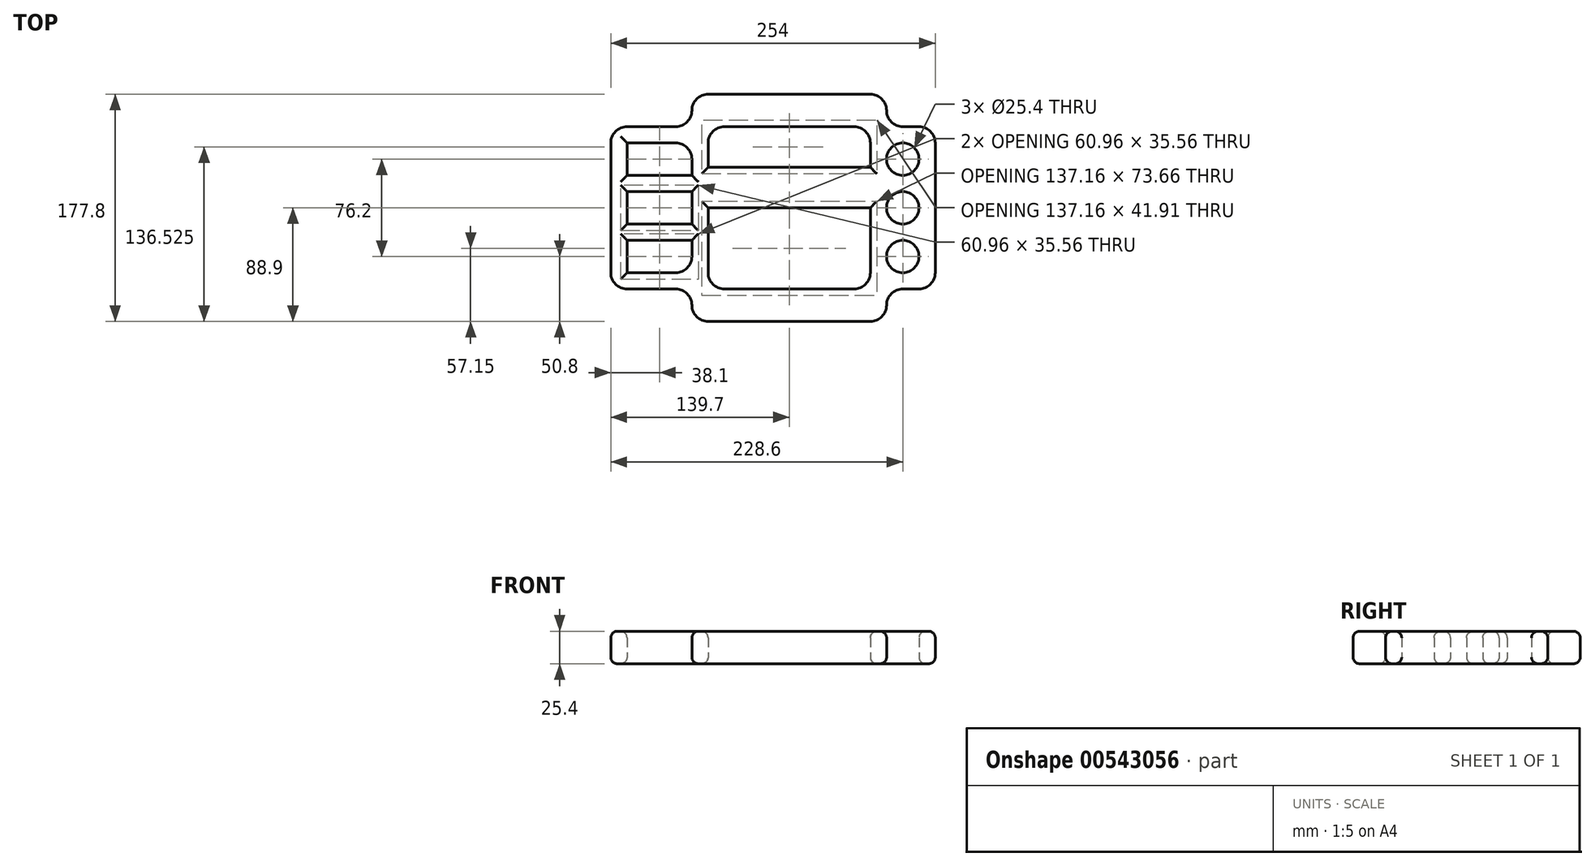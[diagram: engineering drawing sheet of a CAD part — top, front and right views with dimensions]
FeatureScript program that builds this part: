
annotation { "Feature Type Name" : "Feature", "Feature Type Description" : "" }
export const myFeature = defineFeature(function(context is Context, id is Id, definition is map)
    precondition{}
    {
        {
            var Q0;
            Q0=qCreatedBy(makeId("Top.planeOp"),FACE);
            var sketch = newSketch(context, id + "F0", { "sketchPlane" : qUnion([Q0])});
            skLineSegment(sketch, "E0", {"start": v(0, 12.7) * mm, "end": v(0, 12.7) * mm});
            skLineSegment(sketch, "E1", {"start": v(-12.7, 25.4) * mm, "end": v(-50.8, 25.4) * mm});
            skLineSegment(sketch, "E2", {"start": v(-63.5, 38.1) * mm, "end": v(-63.5, 139.7) * mm});
            skLineSegment(sketch, "E3", {"start": v(-50.8, 152.4) * mm, "end": v(-12.7, 152.4) * mm});
            skLineSegment(sketch, "E4", {"start": v(0, 165.1) * mm, "end": v(0, 165.1) * mm});
            skLineSegment(sketch, "E5", {"start": v(12.7, 177.8) * mm, "end": v(139.7, 177.8) * mm});
            skLineSegment(sketch, "E6", {"start": v(152.4, 165.1) * mm, "end": v(152.4, 165.1) * mm});
            skLineSegment(sketch, "E7", {"start": v(165.1, 152.4) * mm, "end": v(177.8, 152.4) * mm});
            skLineSegment(sketch, "E8", {"start": v(190.5, 139.7) * mm, "end": v(190.5, 38.1) * mm});
            skLineSegment(sketch, "E9", {"start": v(177.8, 25.4) * mm, "end": v(165.1, 25.4) * mm});
            skLineSegment(sketch, "E10", {"start": v(152.4, 12.7) * mm, "end": v(152.4, 12.7) * mm});
            skLineSegment(sketch, "E11", {"start": v(139.7, 0) * mm, "end": v(12.7, 0) * mm});
            skPoint(sketch, "E12.visualSharp", {"position": v(0, 177.8) * mm});
            skArc(sketch, "E12.filletArc", {"start": v(12.7, 177.8) * mm, "mid": v(3.72, 174.08) * mm, "end": v(0, 165.1) * mm});
            skPoint(sketch, "E13.visualSharp", {"position": v(152.4, 177.8) * mm});
            skArc(sketch, "E13.filletArc", {"start": v(152.4, 165.1) * mm, "mid": v(148.68, 174.08) * mm, "end": v(139.7, 177.8) * mm});
            skPoint(sketch, "E14.visualSharp", {"position": v(152.4, 152.4) * mm});
            skArc(sketch, "E14.filletArc", {"start": v(152.4, 165.1) * mm, "mid": v(156.12, 156.12) * mm, "end": v(165.1, 152.4) * mm});
            skPoint(sketch, "E15.visualSharp", {"position": v(190.5, 152.4) * mm});
            skArc(sketch, "E15.filletArc", {"start": v(190.5, 139.7) * mm, "mid": v(186.78, 148.68) * mm, "end": v(177.8, 152.4) * mm});
            skPoint(sketch, "E16.visualSharp", {"position": v(190.5, 25.4) * mm});
            skArc(sketch, "E16.filletArc", {"start": v(177.8, 25.4) * mm, "mid": v(186.78, 29.12) * mm, "end": v(190.5, 38.1) * mm});
            skPoint(sketch, "E17.visualSharp", {"position": v(152.4, 25.4) * mm});
            skArc(sketch, "E17.filletArc", {"start": v(165.1, 25.4) * mm, "mid": v(156.12, 21.68) * mm, "end": v(152.4, 12.7) * mm});
            skPoint(sketch, "E18.visualSharp", {"position": v(152.4, 0) * mm});
            skArc(sketch, "E18.filletArc", {"start": v(139.7, 0) * mm, "mid": v(148.68, 3.72) * mm, "end": v(152.4, 12.7) * mm});
            skPoint(sketch, "E19.visualSharp", {"position": v(0, 0) * mm});
            skArc(sketch, "E19.filletArc", {"start": v(0, 12.7) * mm, "mid": v(3.72, 3.72) * mm, "end": v(12.7, 0) * mm});
            skPoint(sketch, "E20.visualSharp", {"position": v(0, 25.4) * mm});
            skArc(sketch, "E20.filletArc", {"start": v(0, 12.7) * mm, "mid": v(-3.72, 21.68) * mm, "end": v(-12.7, 25.4) * mm});
            skPoint(sketch, "E21.visualSharp", {"position": v(-63.5, 25.4) * mm});
            skArc(sketch, "E21.filletArc", {"start": v(-63.5, 38.1) * mm, "mid": v(-59.78, 29.12) * mm, "end": v(-50.8, 25.4) * mm});
            skPoint(sketch, "E22.visualSharp", {"position": v(-63.5, 152.4) * mm});
            skArc(sketch, "E22.filletArc", {"start": v(-50.8, 152.4) * mm, "mid": v(-59.78, 148.68) * mm, "end": v(-63.5, 139.7) * mm});
            skPoint(sketch, "E23.visualSharp", {"position": v(0, 152.4) * mm});
            skArc(sketch, "E23.filletArc", {"start": v(-12.7, 152.4) * mm, "mid": v(-3.72, 156.12) * mm, "end": v(0, 165.1) * mm});
            skCircle(sketch, "E24", {"center": v(165.1, 88.9) * mm, "radius": 12.7 * mm});
            skPoint(sketch, "E24.centerSnap0", {"position": v(190.5, 88.9) * mm});
            skCircle(sketch, "E25", {"center": v(165.1, 127) * mm, "radius": 12.7 * mm});
            skCircle(sketch, "E26", {"center": v(165.1, 50.8) * mm, "radius": 12.7 * mm});
            skLineSegment(sketch, "E27.bottom", {"start": v(-50.8, 38.1) * mm, "end": v(-12.7, 38.1) * mm});
            skLineSegment(sketch, "E27.top", {"start": v(-50.8, 63.5) * mm, "end": v(0, 63.5) * mm});
            skLineSegment(sketch, "E27.left", {"start": v(-50.8, 38.1) * mm, "end": v(-50.8, 63.5) * mm});
            skLineSegment(sketch, "E27.right", {"start": v(0, 50.8) * mm, "end": v(0, 63.5) * mm});
            skLineSegment(sketch, "E28.bottom", {"start": v(-50.8, 101.6) * mm, "end": v(0, 101.6) * mm});
            skLineSegment(sketch, "E28.top", {"start": v(-50.8, 76.2) * mm, "end": v(0, 76.2) * mm});
            skLineSegment(sketch, "E28.left", {"start": v(-50.8, 101.6) * mm, "end": v(-50.8, 76.2) * mm});
            skLineSegment(sketch, "E28.right", {"start": v(0, 101.6) * mm, "end": v(0, 76.2) * mm});
            skLineSegment(sketch, "E29.bottom", {"start": v(-50.8, 139.7) * mm, "end": v(-12.7, 139.7) * mm});
            skLineSegment(sketch, "E29.top", {"start": v(-50.8, 114.3) * mm, "end": v(0, 114.3) * mm});
            skLineSegment(sketch, "E29.left", {"start": v(-50.8, 139.7) * mm, "end": v(-50.8, 114.3) * mm});
            skLineSegment(sketch, "E29.right", {"start": v(0, 127) * mm, "end": v(0, 114.3) * mm});
            skPoint(sketch, "E30.visualSharp", {"position": v(0, 139.7) * mm});
            skArc(sketch, "E30.filletArc", {"start": v(0, 127) * mm, "mid": v(-3.72, 135.98) * mm, "end": v(-12.7, 139.7) * mm});
            skPoint(sketch, "E31.visualSharp", {"position": v(0, 38.1) * mm});
            skArc(sketch, "E31.filletArc", {"start": v(-12.7, 38.1) * mm, "mid": v(-3.72, 41.82) * mm, "end": v(0, 50.8) * mm});
            skLineSegment(sketch, "E32.bottom", {"start": v(12.7, 120.65) * mm, "end": v(139.7, 120.65) * mm});
            skLineSegment(sketch, "E32.top", {"start": v(25.4, 152.4) * mm, "end": v(127, 152.4) * mm});
            skLineSegment(sketch, "E32.left", {"start": v(12.7, 120.65) * mm, "end": v(12.7, 139.7) * mm});
            skLineSegment(sketch, "E32.right", {"start": v(139.7, 120.65) * mm, "end": v(139.7, 139.7) * mm});
            skLineSegment(sketch, "E33.bottom", {"start": v(12.7, 88.9) * mm, "end": v(139.7, 88.9) * mm});
            skLineSegment(sketch, "E33.top", {"start": v(25.4, 25.4) * mm, "end": v(127, 25.4) * mm});
            skLineSegment(sketch, "E33.left", {"start": v(12.7, 88.9) * mm, "end": v(12.7, 38.1) * mm});
            skLineSegment(sketch, "E33.right", {"start": v(139.7, 88.9) * mm, "end": v(139.7, 38.1) * mm});
            skPoint(sketch, "E34.visualSharp", {"position": v(12.7, 25.4) * mm});
            skArc(sketch, "E34.filletArc", {"start": v(12.7, 38.1) * mm, "mid": v(16.42, 29.12) * mm, "end": v(25.4, 25.4) * mm});
            skPoint(sketch, "E35.visualSharp", {"position": v(139.7, 25.4) * mm});
            skArc(sketch, "E35.filletArc", {"start": v(127, 25.4) * mm, "mid": v(135.98, 29.12) * mm, "end": v(139.7, 38.1) * mm});
            skPoint(sketch, "E36.visualSharp", {"position": v(12.7, 152.4) * mm});
            skArc(sketch, "E36.filletArc", {"start": v(25.4, 152.4) * mm, "mid": v(16.42, 148.68) * mm, "end": v(12.7, 139.7) * mm});
            skPoint(sketch, "E37.visualSharp", {"position": v(139.7, 152.4) * mm});
            skArc(sketch, "E37.filletArc", {"start": v(139.7, 139.7) * mm, "mid": v(135.98, 148.68) * mm, "end": v(127, 152.4) * mm});
            skPoint(sketch, "E38.visualSharp", {"position": v(12.7, 88.9) * mm});
            skLineSegment(sketch, "E38.filletArc", {"start": v(12.7, 88.9) * mm, "end": v(12.7, 88.9) * mm});
            skSolve(sketch);
        }
        {
            var Q0;
            Q0=makeQuery(id+"F0.imprint","IMPRINT",FACE,{"disambiguationData":[TD([[makeQuery(id+"F0.imprint","IMPRINT",EDGE,{"derivedFrom":sQuery(id+"F0.wireOp",EDGE,"E1")}),-1.0]])]});
            extrude(context, id + "F1", {"entities" : qUnion([Q0]), "depth" : 25.4 * mm, "offsetDistance" : 25.4 * mm});
        }
        {
            var Q0;
            Q0=makeQuery(id+"F1.opExtrude","CAP_FACE",FACE,{"disambiguationData":[OSD([sQuery(id+"F0.wireOp",EDGE,"E1"),sQuery(id+"F0.wireOp",EDGE,"E2"),sQuery(id+"F0.wireOp",EDGE,"E3"),sQuery(id+"F0.wireOp",EDGE,"E5"),sQuery(id+"F0.wireOp",EDGE,"E7"),sQuery(id+"F0.wireOp",EDGE,"E8"),sQuery(id+"F0.wireOp",EDGE,"E9"),sQuery(id+"F0.wireOp",EDGE,"E11"),sQuery(id+"F0.wireOp",EDGE,"E12.filletArc"),sQuery(id+"F0.wireOp",EDGE,"E13.filletArc"),sQuery(id+"F0.wireOp",EDGE,"E14.filletArc"),sQuery(id+"F0.wireOp",EDGE,"E15.filletArc"),sQuery(id+"F0.wireOp",EDGE,"E16.filletArc"),sQuery(id+"F0.wireOp",EDGE,"E17.filletArc"),sQuery(id+"F0.wireOp",EDGE,"E18.filletArc"),sQuery(id+"F0.wireOp",EDGE,"E19.filletArc"),sQuery(id+"F0.wireOp",EDGE,"E20.filletArc"),sQuery(id+"F0.wireOp",EDGE,"E21.filletArc"),sQuery(id+"F0.wireOp",EDGE,"E22.filletArc"),sQuery(id+"F0.wireOp",EDGE,"E23.filletArc"),sQuery(id+"F0.wireOp",EDGE,"E24"),sQuery(id+"F0.wireOp",EDGE,"E25"),sQuery(id+"F0.wireOp",EDGE,"E26"),sQuery(id+"F0.wireOp",EDGE,"E27.bottom"),sQuery(id+"F0.wireOp",EDGE,"E27.top"),sQuery(id+"F0.wireOp",EDGE,"E27.left"),sQuery(id+"F0.wireOp",EDGE,"E27.right"),sQuery(id+"F0.wireOp",EDGE,"E28.bottom"),sQuery(id+"F0.wireOp",EDGE,"E28.top"),sQuery(id+"F0.wireOp",EDGE,"E28.left"),sQuery(id+"F0.wireOp",EDGE,"E28.right"),sQuery(id+"F0.wireOp",EDGE,"E29.bottom"),sQuery(id+"F0.wireOp",EDGE,"E29.top"),sQuery(id+"F0.wireOp",EDGE,"E29.left"),sQuery(id+"F0.wireOp",EDGE,"E29.right"),sQuery(id+"F0.wireOp",EDGE,"E30.filletArc"),sQuery(id+"F0.wireOp",EDGE,"E31.filletArc"),sQuery(id+"F0.wireOp",EDGE,"E32.bottom"),sQuery(id+"F0.wireOp",EDGE,"E32.top"),sQuery(id+"F0.wireOp",EDGE,"E32.left"),sQuery(id+"F0.wireOp",EDGE,"E32.right"),sQuery(id+"F0.wireOp",EDGE,"E33.bottom"),sQuery(id+"F0.wireOp",EDGE,"E33.top"),sQuery(id+"F0.wireOp",EDGE,"E33.left"),sQuery(id+"F0.wireOp",EDGE,"E33.right"),sQuery(id+"F0.wireOp",EDGE,"E34.filletArc"),sQuery(id+"F0.wireOp",EDGE,"E35.filletArc"),sQuery(id+"F0.wireOp",EDGE,"E36.filletArc"),sQuery(id+"F0.wireOp",EDGE,"E37.filletArc")])],"isStart":false});
            fillet(context, id + "F2", {"entities" : qUnion([Q0]), "radius" : 5.08 * mm, "tangentPropagation" : true, "allowEdgeOverflow" : false});
        }
        {
            var Q0;
            Q0=makeQuery(id+"F1.opExtrude","CAP_FACE",FACE,{"disambiguationData":[OSD([sQuery(id+"F0.wireOp",EDGE,"E1"),sQuery(id+"F0.wireOp",EDGE,"E2"),sQuery(id+"F0.wireOp",EDGE,"E3"),sQuery(id+"F0.wireOp",EDGE,"E5"),sQuery(id+"F0.wireOp",EDGE,"E7"),sQuery(id+"F0.wireOp",EDGE,"E8"),sQuery(id+"F0.wireOp",EDGE,"E9"),sQuery(id+"F0.wireOp",EDGE,"E11"),sQuery(id+"F0.wireOp",EDGE,"E12.filletArc"),sQuery(id+"F0.wireOp",EDGE,"E13.filletArc"),sQuery(id+"F0.wireOp",EDGE,"E14.filletArc"),sQuery(id+"F0.wireOp",EDGE,"E15.filletArc"),sQuery(id+"F0.wireOp",EDGE,"E16.filletArc"),sQuery(id+"F0.wireOp",EDGE,"E17.filletArc"),sQuery(id+"F0.wireOp",EDGE,"E18.filletArc"),sQuery(id+"F0.wireOp",EDGE,"E19.filletArc"),sQuery(id+"F0.wireOp",EDGE,"E20.filletArc"),sQuery(id+"F0.wireOp",EDGE,"E21.filletArc"),sQuery(id+"F0.wireOp",EDGE,"E22.filletArc"),sQuery(id+"F0.wireOp",EDGE,"E23.filletArc"),sQuery(id+"F0.wireOp",EDGE,"E24"),sQuery(id+"F0.wireOp",EDGE,"E25"),sQuery(id+"F0.wireOp",EDGE,"E26"),sQuery(id+"F0.wireOp",EDGE,"E27.bottom"),sQuery(id+"F0.wireOp",EDGE,"E27.top"),sQuery(id+"F0.wireOp",EDGE,"E27.left"),sQuery(id+"F0.wireOp",EDGE,"E27.right"),sQuery(id+"F0.wireOp",EDGE,"E28.bottom"),sQuery(id+"F0.wireOp",EDGE,"E28.top"),sQuery(id+"F0.wireOp",EDGE,"E28.left"),sQuery(id+"F0.wireOp",EDGE,"E28.right"),sQuery(id+"F0.wireOp",EDGE,"E29.bottom"),sQuery(id+"F0.wireOp",EDGE,"E29.top"),sQuery(id+"F0.wireOp",EDGE,"E29.left"),sQuery(id+"F0.wireOp",EDGE,"E29.right"),sQuery(id+"F0.wireOp",EDGE,"E30.filletArc"),sQuery(id+"F0.wireOp",EDGE,"E31.filletArc"),sQuery(id+"F0.wireOp",EDGE,"E32.bottom"),sQuery(id+"F0.wireOp",EDGE,"E32.top"),sQuery(id+"F0.wireOp",EDGE,"E32.left"),sQuery(id+"F0.wireOp",EDGE,"E32.right"),sQuery(id+"F0.wireOp",EDGE,"E33.bottom"),sQuery(id+"F0.wireOp",EDGE,"E33.top"),sQuery(id+"F0.wireOp",EDGE,"E33.left"),sQuery(id+"F0.wireOp",EDGE,"E33.right"),sQuery(id+"F0.wireOp",EDGE,"E34.filletArc"),sQuery(id+"F0.wireOp",EDGE,"E35.filletArc"),sQuery(id+"F0.wireOp",EDGE,"E36.filletArc"),sQuery(id+"F0.wireOp",EDGE,"E37.filletArc")])],"isStart":true});
            fillet(context, id + "F3", {"entities" : qUnion([Q0]), "radius" : 5.08 * mm, "tangentPropagation" : true, "allowEdgeOverflow" : false});
        }
    });
